# Revit family: Toilet-With_Seat-Floor_Mount-KOHLER-Brazn-K-EX22379T_1
name_source: partatom
category: Plumbing Fixtures
units: mm (PartAtom-declared; Revit-internal decimal feet)

## family parameters
Cut with Voids When Loaded = No
Host = Face
OmniClass Number = 23.31.19.00
OmniClass Title = Toilets
Part Type = Normal
Room Calculation Point = No
Round Connector Dimension = Use Diameter
Shared = No

## types (3) — shared parameters
ADA Compliant = No
Assembly Code = D2010100
Bowl Height = 15 9/16"
CW Connection = Yes
Cold Water Inlet = Cold Water Inlet
Date Modified = 07/24/2023
Default Elevation = 0"
Description = IPC Toilet With Slim Queit Close Seat (EXQ) (400MM)
Flow Rate = 0 GPM
Flush Rate- GPF = 0 GPF
Flush Rate- LPF = 0 LPF
HW Connection = No
Height = 29 1/2"
Hot Water Inlet = Hot Water Inlet
Length = 28 7/8"
Manufacturer = Kohler Co.
Master Format 2014 = 22 42 13.13
Master Format 2014 Name = Residential Water Closets
Material = Vitreous China
Pressure = 0.00 psi
Product Name = Brazn
Rough-In = 15 3/4"
Seat Included = Yes
URL = http://www.kohler.com.cn
Vent Connection = No
Waste Connection = Yes
Waste Water Outlet = Waste Water Outlet
WaterSense Certified = No
Width = 14 11/16"

## per-type parameters (varying)
| type | Finish | Model | Type |
| 0-White | Kohler-Vitreous_China-0-White | K-EX22379T-SL-0 | 1 |
| HP1-Peacock | KOHLER-Vitreous_China-HP1-Peacock | K-EX22379T-SL-HP1 | 3 |
| HB1-Honed Black | Kohler-Vitreous_China-HB1-Honed_Black | K-EX22379T-SL-HB1 | 2 |

## geometry (parser evidence)
native form markers: Sweep x6
no freeform markers — native parametric forms only
